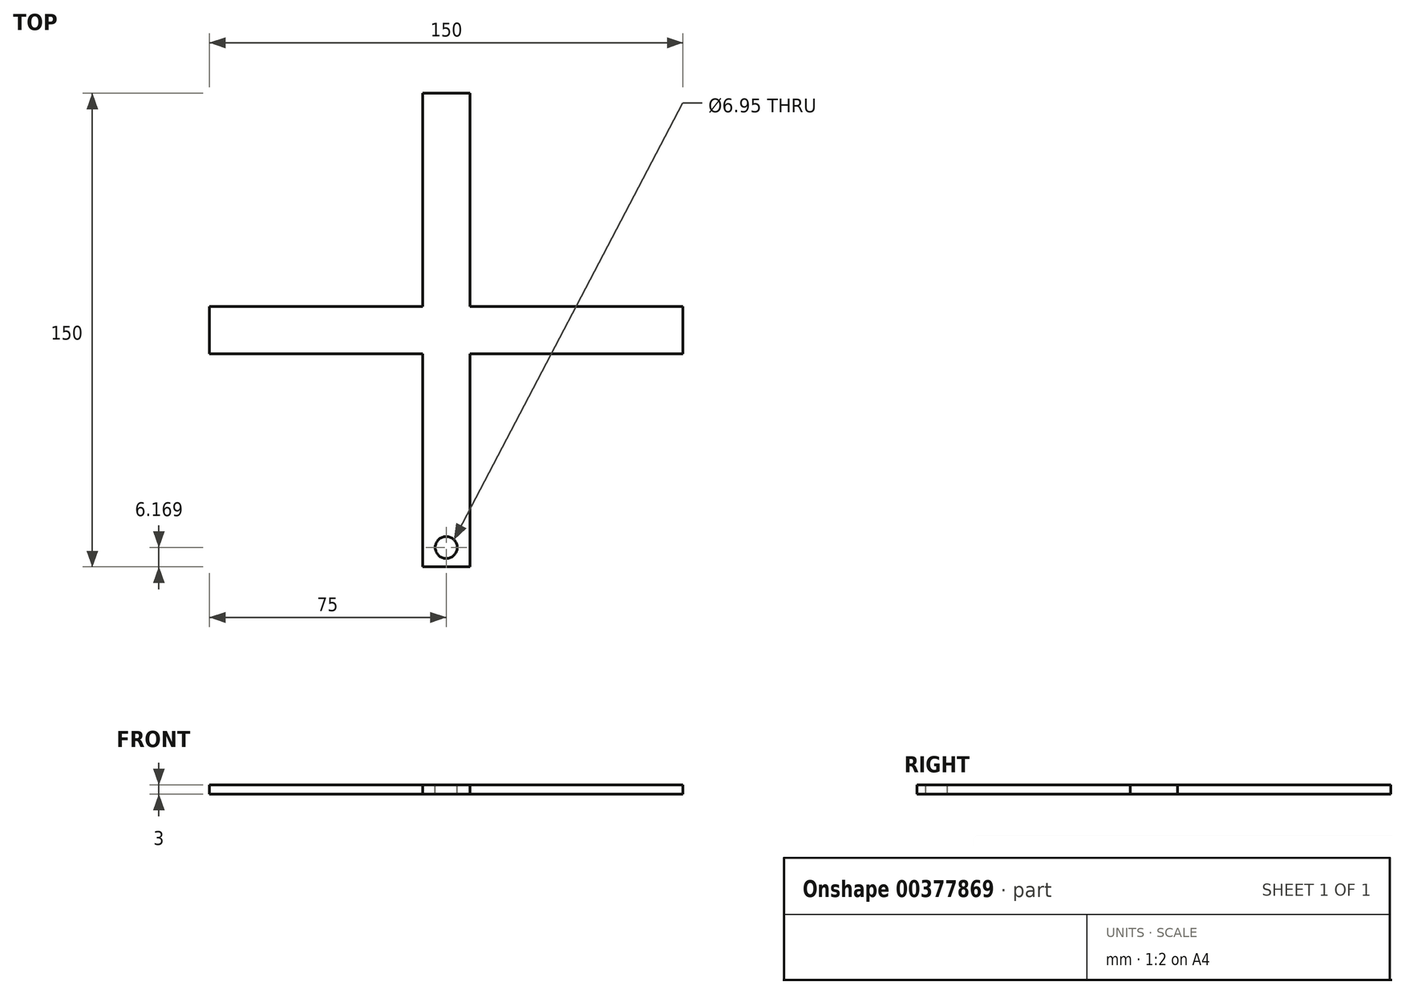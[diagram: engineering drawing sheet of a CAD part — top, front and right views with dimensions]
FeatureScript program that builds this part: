
annotation { "Feature Type Name" : "Feature", "Feature Type Description" : "" }
export const myFeature = defineFeature(function(context is Context, id is Id, definition is map)
    precondition{}
    {
        {
            var Q0;
            Q0=qCreatedBy(makeId("Top.planeOp"),FACE);
            var sketch = newSketch(context, id + "F0", { "sketchPlane" : qUnion([Q0])});
            skLineSegment(sketch, "E0.bottom", {"start": v(75, -7.5) * mm, "end": v(-75, -7.5) * mm});
            skLineSegment(sketch, "E0.top", {"start": v(75, 7.5) * mm, "end": v(-75, 7.5) * mm});
            skLineSegment(sketch, "E0.left", {"start": v(75, -7.5) * mm, "end": v(75, 7.5) * mm});
            skLineSegment(sketch, "E0.right", {"start": v(-75, -7.5) * mm, "end": v(-75, 7.5) * mm});
            skPoint(sketch, "E0.middle", {"position": v(0, 0) * mm});
            skSolve(sketch);
        }
        {
            var Q0;
            Q0=makeQuery(id+"F0.imprint","IMPRINT",FACE,{"disambiguationData":[TD([[makeQuery(id+"F0.imprint","IMPRINT",EDGE,{"derivedFrom":sQuery(id+"F0.wireOp",EDGE,"E0.bottom")}),-1.0]])]});
            extrude(context, id + "F1", {"entities" : qUnion([Q0]), "depth" : 3 * mm});
        }
        {
            var Q0;
            Q0=qCreatedBy(makeId("Top.planeOp"),FACE);
            var sketch = newSketch(context, id + "F2", { "sketchPlane" : qUnion([Q0])});
            skLineSegment(sketch, "E1.bottom", {"start": v(7.5, -75) * mm, "end": v(-7.5, -75) * mm});
            skLineSegment(sketch, "E1.top", {"start": v(7.5, 75) * mm, "end": v(-7.5, 75) * mm});
            skLineSegment(sketch, "E1.left", {"start": v(7.5, -75) * mm, "end": v(7.5, 75) * mm});
            skLineSegment(sketch, "E1.right", {"start": v(-7.5, -75) * mm, "end": v(-7.5, 75) * mm});
            skPoint(sketch, "E1.middle", {"position": v(0, 0) * mm});
            skSolve(sketch);
        }
        {
            var Q0;
            Q0=makeQuery(id+"F2.imprint","IMPRINT",FACE,{"disambiguationData":[TD([[makeQuery(id+"F2.imprint","IMPRINT",EDGE,{"derivedFrom":sQuery(id+"F2.wireOp",EDGE,"E1.bottom")}),-1.0]])]});
            extrude(context, id + "F3", {"entities" : qUnion([Q0]), "operationType" : NewBodyOperationType.ADD, "depth" : 3 * mm});
        }
        {
            var Q0;
            Q0=makeQuery(id+"F3.boolean.opBoolean","MERGE",FACE,{"derivedFrom":[makeQuery(id+"F1.opExtrude","CAP_FACE",FACE,{"disambiguationData":[OSD([sQuery(id+"F0.wireOp",EDGE,"E0.bottom"),sQuery(id+"F0.wireOp",EDGE,"E0.top"),sQuery(id+"F0.wireOp",EDGE,"E0.left"),sQuery(id+"F0.wireOp",EDGE,"E0.right")])],"isStart":false}),makeQuery(id+"F3.opExtrude","CAP_FACE",FACE,{"disambiguationData":[OSD([sQuery(id+"F2.wireOp",EDGE,"E1.bottom"),sQuery(id+"F2.wireOp",EDGE,"E1.top"),sQuery(id+"F2.wireOp",EDGE,"E1.left"),sQuery(id+"F2.wireOp",EDGE,"E1.right")])],"isStart":false})]});
            var sketch = newSketch(context, id + "F4", { "sketchPlane" : qUnion([Q0])});
            skCircle(sketch, "E2", {"center": v(0, -68.83) * mm, "radius": 3.48 * mm});
            skSolve(sketch);
        }
        {
            var Q0;
            Q0=makeQuery(id+"F4.imprint","IMPRINT",FACE,{"disambiguationData":[TD([[makeQuery(id+"F4.imprint","IMPRINT",EDGE,{"derivedFrom":sQuery(id+"F4.wireOp",EDGE,"E2")}),1.0]])]});
            extrude(context, id + "F5", {"entities" : qUnion([Q0]), "operationType" : NewBodyOperationType.REMOVE, "oppositeDirection" : true, "depth" : 25 * mm});
        }
    });
